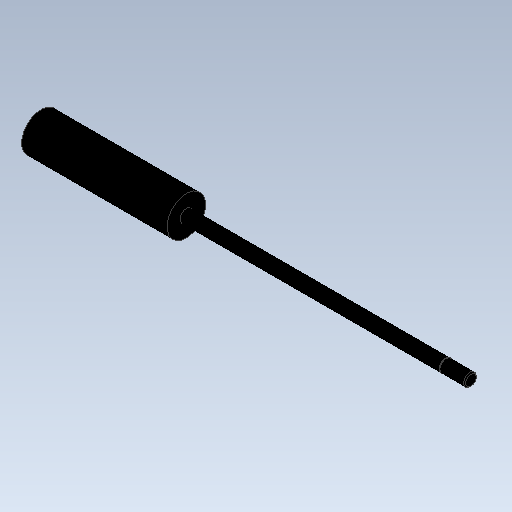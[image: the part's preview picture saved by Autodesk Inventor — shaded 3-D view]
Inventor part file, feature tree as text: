
AUTODESK INVENTOR PART (.ipt)
format: ipt  version: 2020 (Build 240168000, 168)  size: 143,360 bytes
history: native  units: mm (DEFAULTED — no unit token found)
features: other x91, revolve x3, sketch x3
ambient origin geometry x8: Origin, YZ Plane, XZ Plane, XY Plane, X Axis, Y Axis, Z Axis, Center Point
bodies: Solid1 (feature_tree)
feature tree (97):
  revolve  "Revolution1"  Angle=360.0deg
  revolve  "Revolution2"  [1 undecoded]
  revolve  "Revolution3"  [1 undecoded]
  other  "dia1_XY"
  other  "dia1_YZ"
  other  "dia1_ZX"
  other  "dia1_X"
  other  "dia1_Y"
  other  "dia1_Z"
  other  "dia1_Center"
  other  "dia12_XY"
  other  "dia12_YZ"
  other  "dia12_ZX"
  other  "dia12_X"
  other  "dia12_Y"
  other  "dia12_Z"
  other  "dia12_Center"
  other  "dia1r_XY"
  other  "dia1r_YZ"
  other  "dia1r_ZX"
  other  "dia1r_X"
  other  "dia1r_Y"
  other  "dia1r_Z"
  other  "dia1r_Center"
  other  "dia2_XY"
  other  "dia2_YZ"
  other  "dia2_ZX"
  other  "dia2_X"
  other  "dia2_Y"
  other  "dia2_Z"
  other  "dia2_Center"
  other  "dia22_XY"
  other  "dia22_YZ"
  other  "dia22_ZX"
  other  "dia22_X"
  other  "dia22_Y"
  other  "dia22_Z"
  other  "dia22_Center"
  other  "dia2r_XY"
  other  "dia2r_YZ"
  other  "dia2r_ZX"
  other  "dia2r_X"
  other  "dia2r_Y"
  other  "dia2r_Z"
  other  "dia2r_Center"
  other  "rl1_XY"
  other  "rl1_YZ"
  other  "rl1_ZX"
  other  "rl1_X"
  other  "rl1_Y"
  other  "rl1_Z"
  other  "rl1_Center"
  other  "rl2_XY"
  other  "rl2_YZ"
  other  "rl2_ZX"
  other  "rl2_X"
  other  "rl2_Y"
  other  "rl2_Z"
  other  "rl2_Center"
  other  "rod_cp_XY"
  other  "rod_cp_YZ"
  other  "rod_cp_ZX"
  other  "rod_cp_X"
  other  "rod_cp_Y"
  other  "rod_cp_Z"
  other  "rod_cp_Center"
  other  "stroke1_XY"
  other  "stroke1_YZ"
  other  "stroke1_ZX"
  other  "stroke1_X"
  other  "stroke1_Y"
  other  "stroke1_Z"
  other  "stroke1_Center"
  other  "thd1_XY"
  other  "thd1_YZ"
  other  "thd1_ZX"
  other  "thd1_X"
  other  "thd1_Y"
  other  "thd1_Z"
  other  "thd1_Center"
  other  "thd2_XY"
  other  "thd2_YZ"
  other  "thd2_ZX"
  other  "thd2_X"
  other  "thd2_Y"
  other  "thd2_Z"
  other  "thd2_Center"
  other  "to_rod_clevis_XY"
  other  "to_rod_clevis_YZ"
  other  "to_rod_clevis_ZX"
  other  "to_rod_clevis_X"
  other  "to_rod_clevis_Y"
  other  "to_rod_clevis_Z"
  other  "to_rod_clevis_Center"
  sketch  "Sketch_1"  dims[d0=360.0deg d1=360.0deg]
  sketch  "Sketch_3"  dims[d2=360.0deg]
  sketch  "Sketch_30"  dims[d3=0.0mm d4=0.0mm d5=0.0mm d6=0.0mm d7=0.0mm d8=0.0mm]
note: 2 required parameter values undecoded (feature->parameter linkage not recoverable at this tier; creation-order binding heuristic only, values carry confidence <= 0.55)
